# Revit family: Unonovesette_VARIO 40
name_source: partatom
category: Lighting Fixtures
units: mm (PartAtom-declared; Revit-internal decimal feet)

## family parameters
Always vertical = No
Cut with Voids When Loaded = No
Light Source = No
Part Type = Normal
Room Calculation Point = No
Round Connector Dimension = Use Diameter
Shared = No
Work Plane-Based = Yes

## types (1)
- Unonovesette_VARIO 40
    197_Beam_Angle = 10°
    197_Colour = 197_Black_Anodized
    197_Colour_Rendering_Index_CRI = >90
    197_Colour_Temperature = 2200 K
    197_Degree_of_Protection = IP66
    197_Dimension = D45xH102
    197_Impact Protection Rating = IK08
    197_Insulation_Class = III
    197_Lamp = LED
    197_Light_Source = 197_Light_Source
    197_Luminous_Flux = 145 lm
    197_Model = Vario 40
    197_Photometrics = 197_VARIO 40 - Photometrics : V40.22.N.XX.02
    197_Product_Code = V40.22.N.05.02
    197_Rated_Voltage = 0 V
    197_Wattage = 3 W
    197_Weight = 0.27 kg
    Apparent Load = 3 VA
    Default Elevation = 1219 mm
    IfcExportAs = IfcLightFixtureType
    IfcExportType = DIRECTIONSOURCE
    Manufacturer = unonovesette ltd
    Model = Vario 40
    URL = https://unonovesette.it
    Uniclass2015Code = Pr_70_70_48_82
    Uniclass2015Title = Spot lights
    Uniclass2015Version = Product v1.12

## geometry (parser evidence)
native form markers: Blend x4, Sweep x22
no freeform markers — native parametric forms only
